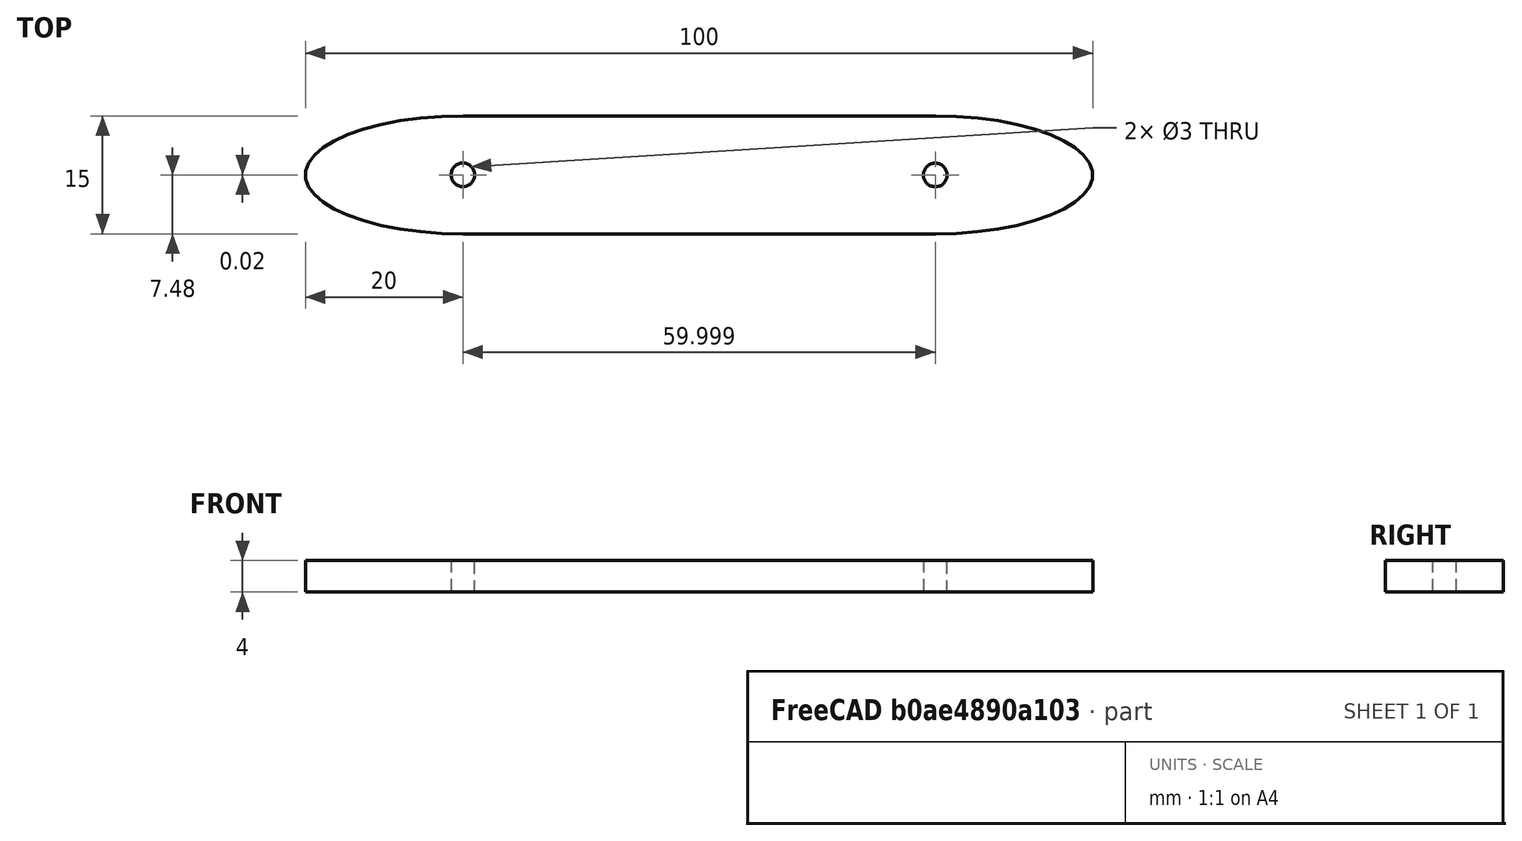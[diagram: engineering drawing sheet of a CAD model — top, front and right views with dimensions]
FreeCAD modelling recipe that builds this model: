
FCSTD DOCUMENT  (FreeCAD 0.16R6706 (Git))
Label: femur
License: All rights reserved
LicenseURL: http://en.wikipedia.org/wiki/All_rights_reserved
objects: Sketcher::SketchObject×1, PartDesign::Pad×1
note: 3 computed .brp shape members not serialized (recipe doc carries the construction recipe); baked Part::Feature solids carry a one-line shape summary decoded from their .brp

FEATURE [Sketcher::SketchObject] Sketch
  sketch-geometry (14):
    g0: ArcOfEllipse CenterX=0 CenterY=0 CenterZ=0 NormalX=0 NormalY=0 NormalZ=1 MajorRadius=20 MinorRadius=7.5 AngleXU=3.14159 StartAngle=4.71239 EndAngle=7.85398
    g1: LineSegment [constr] StartX=-20 StartY=6.2495e-08 StartZ=0 EndX=20 EndY=-6.2495e-08 EndZ=0
    g2: LineSegment [constr] StartX=-2.3436e-08 StartY=-7.5 StartZ=0 EndX=2.3436e-08 EndY=7.5 EndZ=0
    g3: GeomPoint [constr] X=-18.5405 Y=5.7935e-08 Z=0
    g4: GeomPoint [constr] X=18.5405 Y=-5.7935e-08 Z=0
    g5: LineSegment StartX=-4.281e-09 StartY=7.5 StartZ=0 EndX=60 EndY=7.5 EndZ=0
    g6: LineSegment StartX=0 StartY=-7.5 StartZ=0 EndX=60 EndY=-7.5 EndZ=0
    g7: ArcOfEllipse CenterX=60 CenterY=0 CenterZ=0 NormalX=0 NormalY=0 NormalZ=1 MajorRadius=20 MinorRadius=7.5 AngleXU=0 StartAngle=4.71239 EndAngle=7.85398
    g8: LineSegment [constr] StartX=80 StartY=0 StartZ=0 EndX=40 EndY=0 EndZ=0
    g9: LineSegment [constr] StartX=60 StartY=7.5 StartZ=0 EndX=60 EndY=-7.5 EndZ=0
    g10: GeomPoint [constr] X=78.5405 Y=0 Z=0
    g11: GeomPoint [constr] X=41.4595 Y=0 Z=0
    g12: Circle CenterX=59.9992 CenterY=-0.020412 CenterZ=0 NormalX=0 NormalY=0 NormalZ=1 Radius=1.5
    g13: Circle CenterX=0 CenterY=0 CenterZ=0 NormalX=0 NormalY=0 NormalZ=1 Radius=1.5
  constraints (24):
    c: InternalAlignment(g1-g4 -> g0) x4
    c: Coincident(g0,g-1)
    c: PointOnObject(g0,g-2)
    c: Coincident(g5,g0)
    c: Horizontal(g5)
    c: Tangent(g0,g0)
    c: Coincident(g6,g0)
    c: Horizontal(g6)
    c: Tangent(g0,g0)
    c: Tangent(g0,g5)
    c: Tangent(g0,g6)
    c: InternalAlignment(g8-g11 -> g7) x4
    c: Tangent(g7,g6)
    c: Coincident(g6,g7)
    c: Tangent(g7,g5)
    c: Horizontal(g8)
    c: Coincident(g5,g7)
    c: Equal(g8,g1)
    c: DistanceX(g-1,g7) = 60
    c: Distance(g8,g9) = 20
    c: DistanceY(g9,g9) = 15
    c: Radius(g12) = 1.5
    c: Coincident(g13,g-1)
    c: Radius(g13) = 1.5
FEATURE [PartDesign::Pad] Pad
  Length = 4
  Length2 = 100
  Sketch = -> Sketch
  Type = 0
